# Revit family: Qf_Fisher_3042 Faucet Dipperwell
name_source: partatom
category: Specialty Equipment
revit_build: Autodesk Revit 2018 (Build: 20170223_1515(x64)
units: mm (PartAtom-declared; Revit-internal decimal feet)

## family parameters
Always vertical = Yes
Cut with Voids When Loaded = No
Part Type = Normal
Room Calculation Point = No
Round Connector Dimension = Use Diameter
Shared = No
Work Plane-Based = No

## types (1)
- Qf_Fisher_3042 Faucet Dipperwell
    Cold Water Connection Height = 0"
    Cold Water Flow = 3 GPM
    Cold Water Maximum Pressure = 100.00 psi
    Cold Water Minimum Pressure = 60.00 psi
    Cold Water RI Height = 0"
    Cold Water Size = 0"
    Cold Water Temperature Recommended = 160 °F
    Depth = 2 1/4"
    Description = FAUCET DIPPERWELL
    Fixture Finish = QF_Metal - Brass - Polished
    Foodservice Equipment Identifier = Yes
    Height = 2 3/4"
    Identify Quantity as Lot = Yes
    Length = 1 1/2"
    Manufacturer = FISHER
    Model = 3042
    Weight in Pounds = 1

## geometry (parser evidence)
native form markers: Sweep x3
no freeform markers — native parametric forms only
